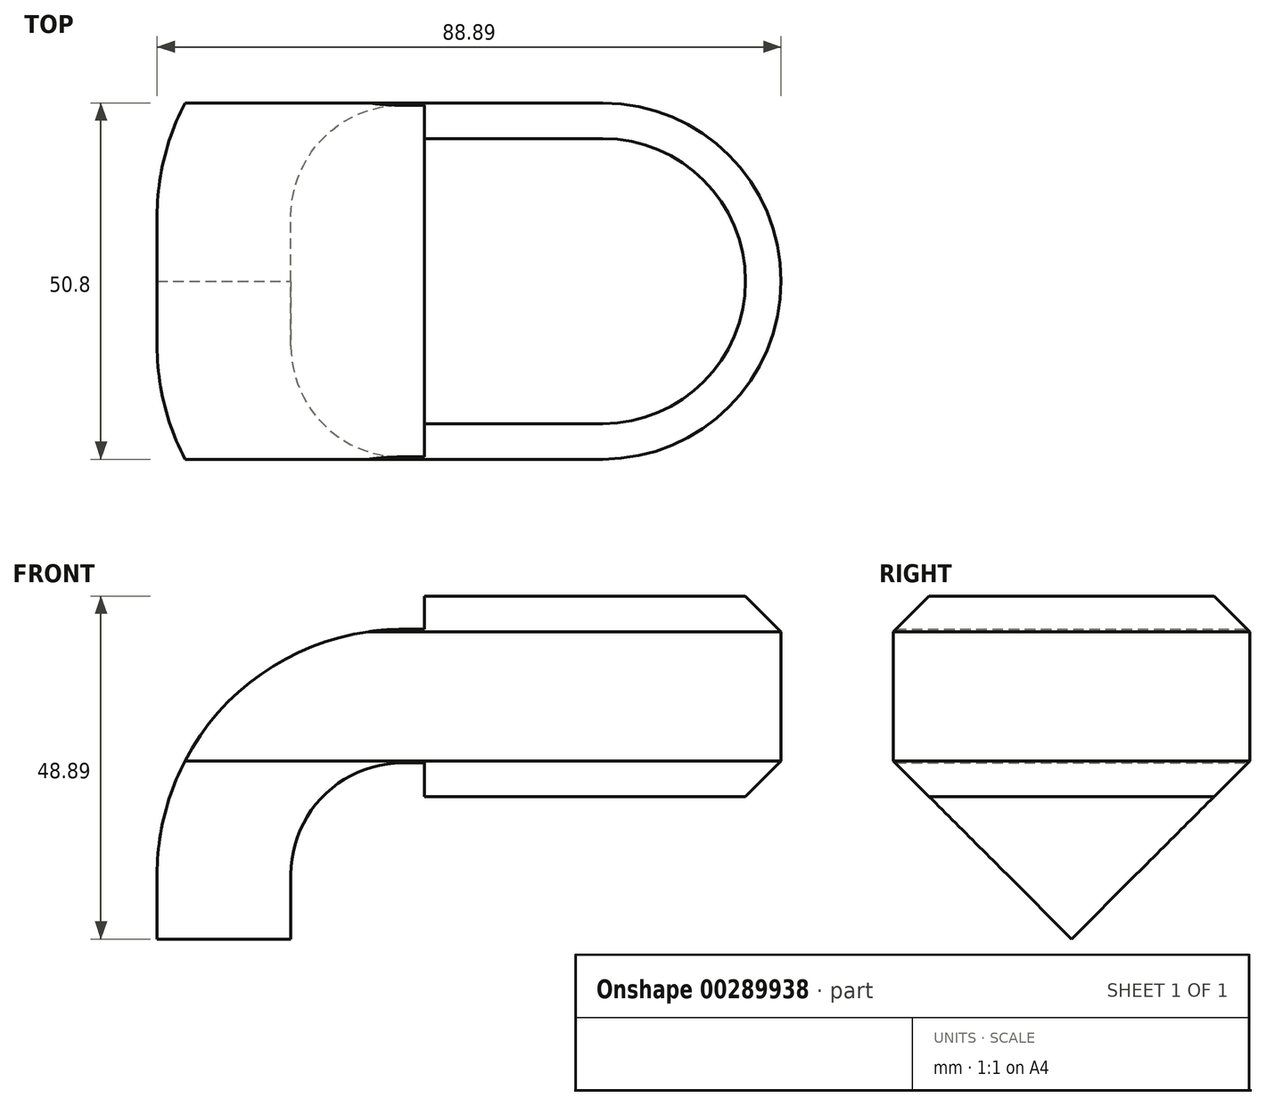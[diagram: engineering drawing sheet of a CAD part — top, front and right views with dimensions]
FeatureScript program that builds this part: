
annotation { "Feature Type Name" : "Feature", "Feature Type Description" : "" }
export const myFeature = defineFeature(function(context is Context, id is Id, definition is map)
    precondition{}
    {
        {
            var Q0;
            Q0=qCreatedBy(makeId("Front.planeOp"),FACE);
            var sketch = newSketch(context, id + "F0", { "sketchPlane" : qUnion([Q0])});
            skLineSegment(sketch, "E0.bottom", {"start": v(41.28, -9.52) * mm, "end": v(-41.28, -9.53) * mm});
            skLineSegment(sketch, "E0.top", {"start": v(41.28, 9.53) * mm, "end": v(-41.28, 9.52) * mm});
            skLineSegment(sketch, "E0.left", {"start": v(41.28, -9.52) * mm, "end": v(41.28, 9.53) * mm});
            skLineSegment(sketch, "E0.right", {"start": v(-41.28, -9.53) * mm, "end": v(-41.28, 9.52) * mm});
            skPoint(sketch, "E0.middle", {"position": v(0, 0) * mm});
            skLineSegment(sketch, "E1.bottom", {"start": v(111.12, 38.1) * mm, "end": v(60.33, 38.1) * mm});
            skLineSegment(sketch, "E1.top", {"start": v(111.12, 66.68) * mm, "end": v(60.33, 66.68) * mm});
            skLineSegment(sketch, "E1.left", {"start": v(111.12, 38.1) * mm, "end": v(111.12, 66.68) * mm});
            skLineSegment(sketch, "E1.right", {"start": v(60.33, 38.1) * mm, "end": v(60.33, 66.68) * mm});
            skPoint(sketch, "E1.middle", {"position": v(85.72, 52.39) * mm});
            skLineSegment(sketch, "E2", {"start": v(41.28, 9.53) * mm, "end": v(41.28, 27) * mm});
            skArc(sketch, "E3", {"start": v(41.28, 27) * mm, "mid": v(45.92, 38.23) * mm, "end": v(57.15, 42.88) * mm});
            skLineSegment(sketch, "E4", {"start": v(57.15, 42.88) * mm, "end": v(85.73, 42.88) * mm});
            skLineSegment(sketch, "E5.0", {"start": v(57.15, 61.93) * mm, "end": v(85.73, 61.93) * mm});
            skArc(sketch, "E5.1", {"start": v(22.23, 27) * mm, "mid": v(32.45, 51.7) * mm, "end": v(57.15, 61.93) * mm});
            skLineSegment(sketch, "E5.2", {"start": v(22.23, 9.53) * mm, "end": v(22.23, 27) * mm});
            skLineSegment(sketch, "E6", {"start": v(85.73, 38.1) * mm, "end": v(85.72, 66.68) * mm});
            skFitSpline(sketch, "E7", {"points": [v(-41.28, 9.52) * mm, v(57.15, 61.93) * mm], "startDerivative": vector(5.17, 102.62) * mm, "endDerivative": vector(153.53, -8.58) * mm});
            skSolve(sketch);
        }
        {
            var Q0;
            Q0=makeQuery(id+"F0.imprint","IMPRINT",FACE,{"disambiguationData":[TD([[makeQuery(id+"F0.imprint","IMPRINT",EDGE,{"derivedFrom":sQuery(id+"F0.wireOp",EDGE,"E0.bottom")}),-1.0]])]});
            extrude(context, id + "F1", {"entities" : qUnion([Q0]), "endBound" : BoundingType.SYMMETRIC, "depth" : 127 * mm});
        }
        {
            var Q0;
            {var subQ1=sQuery(id+"F0.wireOp",EDGE,"E2");Q0=makeQuery(id+"F0.imprint","IMPRINT",FACE,{"disambiguationData":[TD([[makeQuery(id+"F0.imprint","IMPRINT",EDGE,{"derivedFrom":subQ1}),1.0]])]});}
            var Q1;
            {var subQ0=sQuery(id+"F0.wireOp",EDGE,"E4");var subQ1=sQuery(id+"F0.wireOp",EDGE,"E1.right");var subQ2=makeQuery(id+"F0.imprint","INTERSECT",VERTEX,{"derivedFrom":[subQ1,subQ0]});Q1=makeQuery(id+"F0.imprint","IMPRINT",FACE,{"disambiguationData":[TD([[makeQuery(id+"F0.imprint","IMPRINT",EDGE,{"disambiguationData":[TD([[subQ2,-1.0]])],"derivedFrom":subQ1}),-1.0]])]});}
            var Q2;
            {var subQ0=sQuery(id+"F0.wireOp",EDGE,"E1.right");var subQ1=sQuery(id+"F0.wireOp",EDGE,"E1.bottom");var subQ2=makeQuery(id+"F0.imprint","INTERSECT",VERTEX,{"derivedFrom":[subQ1,subQ0]});Q2=makeQuery(id+"F0.imprint","IMPRINT",FACE,{"disambiguationData":[TD([[makeQuery(id+"F0.imprint","IMPRINT",EDGE,{"disambiguationData":[TD([[subQ2,1.0]])],"derivedFrom":subQ1}),-1.0]])]});}
            var Q3;
            {var subQ0=sQuery(id+"F0.wireOp",EDGE,"E1.right");var subQ1=sQuery(id+"F0.wireOp",EDGE,"E1.top");var subQ2=makeQuery(id+"F0.imprint","INTERSECT",VERTEX,{"derivedFrom":[subQ1,subQ0]});Q3=makeQuery(id+"F0.imprint","IMPRINT",FACE,{"disambiguationData":[TD([[makeQuery(id+"F0.imprint","IMPRINT",EDGE,{"disambiguationData":[TD([[subQ2,1.0]])],"derivedFrom":subQ1}),1.0]])]});}
            extrude(context, id + "F2", {"entities" : qUnion([Q0, Q1, Q2, Q3]), "operationType" : NewBodyOperationType.ADD, "endBound" : BoundingType.SYMMETRIC, "depth" : 50.8 * mm});
        }
        {
            var Q0;
            Q0=makeQuery(id+"F0.imprint","IMPRINT",FACE,{"disambiguationData":[TD([[makeQuery(id+"F0.imprint","IMPRINT",EDGE,{"derivedFrom":sQuery(id+"F0.wireOp",EDGE,"E5.1")}),1.0]])]});
            extrude(context, id + "F3", {"entities" : qUnion([Q0]), "operationType" : NewBodyOperationType.ADD, "endBound" : BoundingType.SYMMETRIC, "depth" : 6.35 * mm});
        }
        {
            var Q0;
            {var subQ4=sQuery(id+"F0.wireOp",EDGE,"E1.left");Q0=makeQuery(id+"F0.imprint","IMPRINT",FACE,{"disambiguationData":[TD([[makeQuery(id+"F0.imprint","IMPRINT",EDGE,{"derivedFrom":subQ4}),1.0]])]});}
            var Q1;
            Q1=sQuery(id+"F0.wireOp",EDGE,"E6");
            revolve(context, id + "F4", {"operationType" : NewBodyOperationType.ADD, "entities" : qUnion([Q0]), "axis" : qUnion([Q1]), "revolveType" : RevolveType.FULL});
        }
        {
            var Q0;
            Q0=makeQuery(id+"F4.opRevolve","SWEPT_FACE",FACE,{"disambiguationData":[OSD([sQuery(id+"F0.wireOp",EDGE,"E1.left")])]});
            chamfer(context, id + "F5", {"entities" : qUnion([Q0]), "width" : 5.08 * mm, "tangentPropagation" : true});
        }
    });
